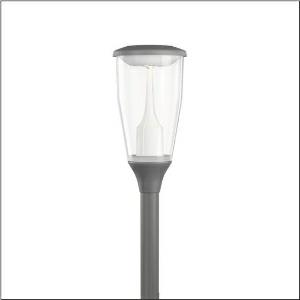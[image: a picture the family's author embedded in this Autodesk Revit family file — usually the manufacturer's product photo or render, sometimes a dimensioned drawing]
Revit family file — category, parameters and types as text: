
# Revit family: dl_11_iq___p1_0a_5xa5575ff14hp00022_3c96
name_source: partatom
category: Lighting Fixtures
units: mm (PartAtom-declared; Revit-internal decimal feet)

## family parameters
Cut with Voids When Loaded = No
Host = Face
Light Source = No
Part Type = Normal
Room Calculation Point = No
Round Connector Dimension = Use Diameter
Shared = No

## types (1)
- --- (1 x LED, 4780 lm, 33.6 W, 3000K)
    Apparent Load = 34 VA
    CIE Flux Codes = 33 63 91 94 100
    Color Rendering = 70
    Color Temperature = 3000K
    Default Elevation = 1800 mm
    Description = DL 11 iQ, mast luminaire, Module 540 iQ-SR, primary light control with 3 zone facetted reflector, of plastic, silver coated, highly specular, structured, primary optical cover: cover, of PMMA, transparent, light distribution: P1.0a, light emission: direct distribution, primary light characteristic: asymmetric, installation type: post-top, LED, High Power LED, light colour: 730, colour temperature: 3000K, control gear: iQ Street-Remote, control: Street-Remote, Auto-Match, Temp-Guard, Lumen-Switch, Night-Set, Smart-Wire, Light-Fading, Desk-Remote (wireless, voltage-free reading and setting of iQ features in the workshop via application-optimized NFC function/RFID function), optimised constant luminous flux control (CLO 2.0), mains connection: 220..240V, AC, 50/60Hz, connection cable pre-assembled, cable length: 5,5m, wiring characteristics: H07RN-F, 5-core, 1.5mm², start of lifetime: 34W, end of service life: 36W, luminaire housing, upper part, of diecast aluminium, coated, SITECO metallic grey (DB 702S), spigot size: 76mm (post-top), mounting height: 3..5m, post-top mast mounting element, of diecast aluminium, coated, SITECO metallic grey (DB 702S), Module 540 iQ-SR, traffic white (RAL 9016), equipment: Power, protection rating (complete): IP66, insulation class (complete): insulation class II (safety insulation), certification: CE, ENEC, ENEC+, VDE, impact resistance: IK07, packaging unit: 1 piece

Light Distribution: P1.0a
    Height = 665 mm
    Lamp = 1 x LED
    Lamp Light Flux = 4780 lm
    Lamp Power = 33.6 W
    Lamp count = 1
    Length = 334 mm
    Luminous efficacy = 142 lm/W
    Manufacturer = Siteco
    ModVariant = No
    Model = 5XA5575FF14HP00022
    Number of Poles = 1
    OnlyDefault = Yes
    Power Factor = 1
    Product Name = DL 11 iQ | P1.0a
    Product group = mast luminaire | pylon top
    ProductGroupID = 6100
    Protection Class = Protection class II
    Protection Degree = IP 66
    RLX_Detail_Level = 1
    RLX_Emergency_Light_Flux = 0 lm
    RLX_Emergency_Type = 0
    RLX_Emergency_Type_DB = No
    RlxData = <blob elided: 104569 chars, md5=b0e8cfc1>
    Socket = socket
    Standby Power = 0 W
    System Light Flux = 4780 lm
    System Power = 34 W
    Type Comments = factory setting: luminous flux: 100 % | dim-lin: 254 | 695 mA
    Type Image = l_1258354.jpg
    URL = http://relux.com
    VarID = @adj_039855
    Voltage = 0 V
    Weight = 0.00 kg
    Width = 0 mm  [stored 0 ft]

note: [stored X ft] marks values corroborated as IEEE doubles in the binary element streams (Revit-internal decimal feet)

## geometry (parser evidence)
native form markers: Blend x4, Sweep x10
no freeform markers — native parametric forms only
